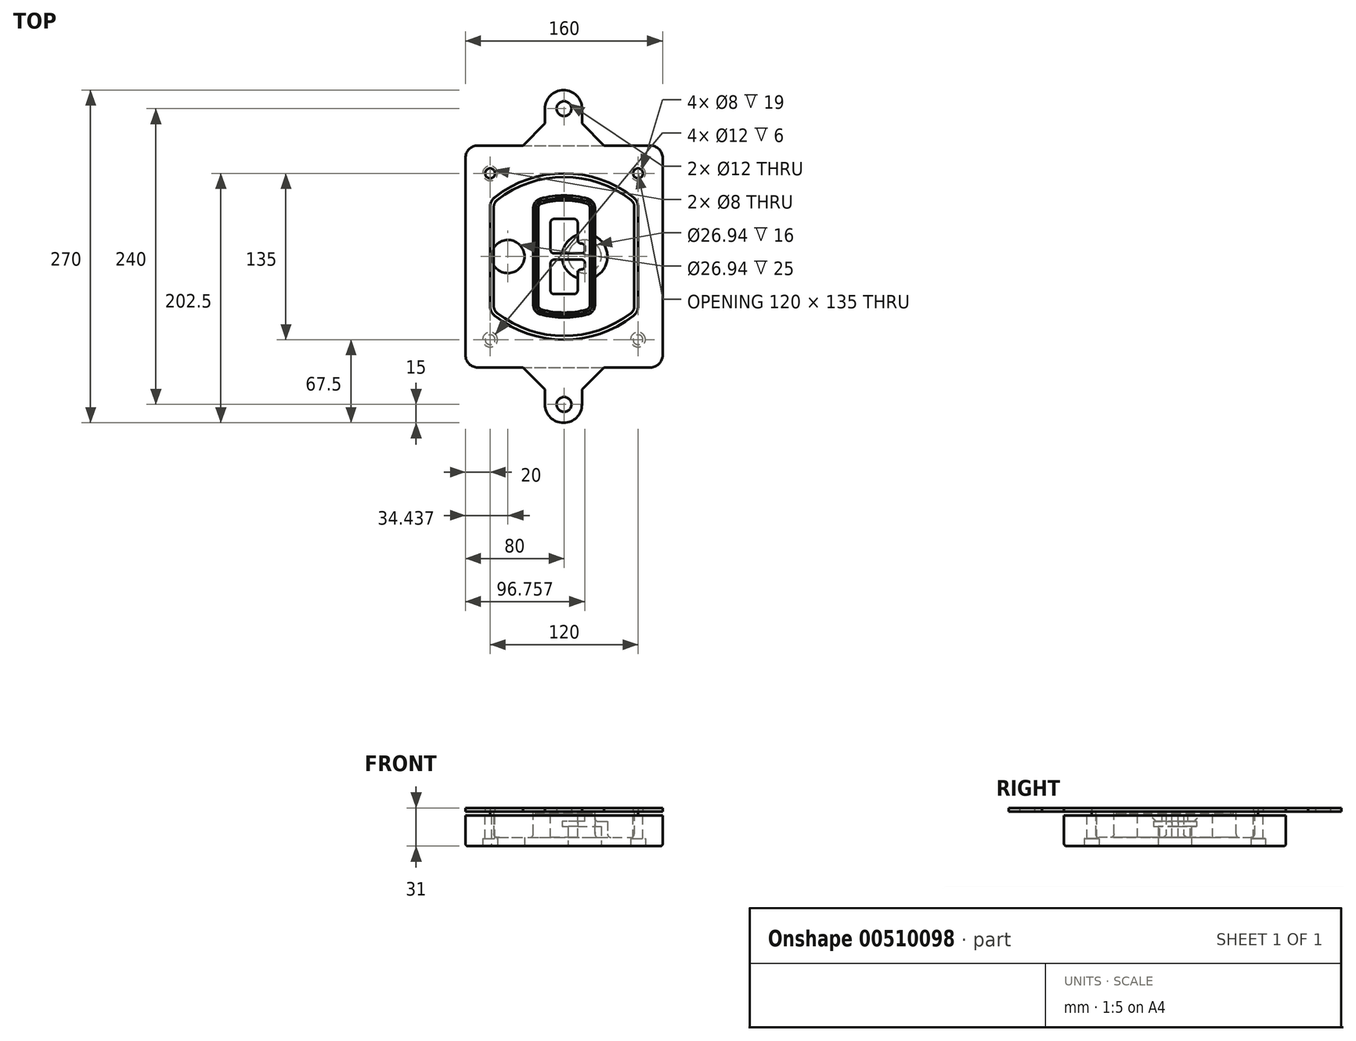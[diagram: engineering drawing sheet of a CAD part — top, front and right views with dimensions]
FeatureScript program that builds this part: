
annotation { "Feature Type Name" : "Feature", "Feature Type Description" : "" }
export const myFeature = defineFeature(function(context is Context, id is Id, definition is map)
    precondition{}
    {
        {
            var Q0;
            Q0=qCreatedBy(makeId("Top.planeOp"),FACE);
            var sketch = newSketch(context, id + "F0", { "sketchPlane" : qUnion([Q0])});
            skPoint(sketch, "E0.rect.middle", {"position": v(0, 0) * mm});
            skLineSegment(sketch, "E1.bottom", {"start": v(-70, -90) * mm, "end": v(70, -90) * mm});
            skLineSegment(sketch, "E1.top", {"start": v(-70, 90) * mm, "end": v(70, 90) * mm});
            skLineSegment(sketch, "E1.left", {"start": v(-80, -80) * mm, "end": v(-80, 80) * mm});
            skLineSegment(sketch, "E1.right", {"start": v(80, -80) * mm, "end": v(80, 80) * mm});
            skLineSegment(sketch, "E2", {"start": v(-80, 90) * mm, "end": v(80, -90) * mm, "construction": true});
            skLineSegment(sketch, "E3", {"start": v(80, 90) * mm, "end": v(-80, -90) * mm, "construction": true});
            skCircle(sketch, "E4", {"center": v(-60, 67.5) * mm, "radius": 4 * mm});
            skCircle(sketch, "E5", {"center": v(60, 67.5) * mm, "radius": 4 * mm});
            skCircle(sketch, "E6", {"center": v(60, -67.5) * mm, "radius": 4 * mm});
            skCircle(sketch, "E7", {"center": v(-60, -67.5) * mm, "radius": 4 * mm});
            skLineSegment(sketch, "E8", {"start": v(-60, 67.5) * mm, "end": v(60, 67.5) * mm, "construction": true});
            skLineSegment(sketch, "E9", {"start": v(60, 67.5) * mm, "end": v(60, -67.5) * mm, "construction": true});
            skLineSegment(sketch, "E10", {"start": v(60, -67.5) * mm, "end": v(-60, -67.5) * mm, "construction": true});
            skLineSegment(sketch, "E11", {"start": v(-60, -67.5) * mm, "end": v(-60, 67.5) * mm, "construction": true});
            skLineSegment(sketch, "E12", {"start": v(-60, 40.3) * mm, "end": v(-60, -40.3) * mm});
            skLineSegment(sketch, "E13", {"start": v(60, 40.3) * mm, "end": v(60, -40.3) * mm});
            skArc(sketch, "E14", {"start": v(56.15, 48.18) * mm, "mid": v(0, 67.5) * mm, "end": v(-56.15, 48.18) * mm});
            skArc(sketch, "E15", {"start": v(-56.15, -48.18) * mm, "mid": v(0, -67.5) * mm, "end": v(56.15, -48.18) * mm});
            skLineSegment(sketch, "E16", {"start": v(-60, 0) * mm, "end": v(60, 0) * mm, "construction": true});
            skPoint(sketch, "E17.visualSharp", {"position": v(-60, -45) * mm});
            skArc(sketch, "E17.filletArc", {"start": v(-60, -40.3) * mm, "mid": v(-58.99, -44.68) * mm, "end": v(-56.15, -48.18) * mm});
            skPoint(sketch, "E18.visualSharp", {"position": v(-60, 45) * mm});
            skArc(sketch, "E18.filletArc", {"start": v(-56.15, 48.18) * mm, "mid": v(-58.99, 44.68) * mm, "end": v(-60, 40.3) * mm});
            skPoint(sketch, "E19.visualSharp", {"position": v(60, 45) * mm});
            skArc(sketch, "E19.filletArc", {"start": v(60, 40.3) * mm, "mid": v(58.99, 44.68) * mm, "end": v(56.15, 48.18) * mm});
            skPoint(sketch, "E20.visualSharp", {"position": v(60, -45) * mm});
            skArc(sketch, "E20.filletArc", {"start": v(56.15, -48.18) * mm, "mid": v(58.99, -44.68) * mm, "end": v(60, -40.3) * mm});
            skPoint(sketch, "E21.visualSharp", {"position": v(-80, 90) * mm});
            skArc(sketch, "E21.filletArc", {"start": v(-70, 90) * mm, "mid": v(-77.07, 87.07) * mm, "end": v(-80, 80) * mm});
            skPoint(sketch, "E22.visualSharp", {"position": v(80, 90) * mm});
            skArc(sketch, "E22.filletArc", {"start": v(80, 80) * mm, "mid": v(77.07, 87.07) * mm, "end": v(70, 90) * mm});
            skPoint(sketch, "E23.visualSharp", {"position": v(80, -90) * mm});
            skArc(sketch, "E23.filletArc", {"start": v(70, -90) * mm, "mid": v(77.07, -87.07) * mm, "end": v(80, -80) * mm});
            skPoint(sketch, "E24.visualSharp", {"position": v(-80, -90) * mm});
            skArc(sketch, "E24.filletArc", {"start": v(-80, -80) * mm, "mid": v(-77.07, -87.07) * mm, "end": v(-70, -90) * mm});
            skArc(sketch, "E25.0", {"start": v(57, 40.3) * mm, "mid": v(56.3, 43.36) * mm, "end": v(54.3, 45.81) * mm});
            skLineSegment(sketch, "E25.1", {"start": v(57, 40.3) * mm, "end": v(57, -40.3) * mm});
            skArc(sketch, "E25.2", {"start": v(54.3, -45.81) * mm, "mid": v(56.3, -43.36) * mm, "end": v(57, -40.3) * mm});
            skArc(sketch, "E25.3", {"start": v(-54.3, -45.81) * mm, "mid": v(0, -64.5) * mm, "end": v(54.3, -45.81) * mm});
            skArc(sketch, "E25.4", {"start": v(-57, -40.3) * mm, "mid": v(-56.3, -43.36) * mm, "end": v(-54.3, -45.81) * mm});
            skArc(sketch, "E25.5", {"start": v(54.3, 45.81) * mm, "mid": v(0, 64.5) * mm, "end": v(-54.3, 45.81) * mm});
            skLineSegment(sketch, "E25.6", {"start": v(-57, 40.3) * mm, "end": v(-57, -40.3) * mm});
            skArc(sketch, "E25.7", {"start": v(-54.3, 45.81) * mm, "mid": v(-56.3, 43.36) * mm, "end": v(-57, 40.3) * mm});
            skArc(sketch, "E26.0", {"start": v(-58.62, 51.33) * mm, "mid": v(-62.58, 46.43) * mm, "end": v(-64, 40.3) * mm});
            skArc(sketch, "E26.1", {"start": v(58.62, 51.33) * mm, "mid": v(0, 71.5) * mm, "end": v(-58.62, 51.33) * mm});
            skArc(sketch, "E26.2", {"start": v(64, 40.3) * mm, "mid": v(62.58, 46.43) * mm, "end": v(58.62, 51.33) * mm});
            skLineSegment(sketch, "E26.3", {"start": v(64, 40.3) * mm, "end": v(64, -40.3) * mm});
            skArc(sketch, "E26.4", {"start": v(58.62, -51.33) * mm, "mid": v(62.58, -46.43) * mm, "end": v(64, -40.3) * mm});
            skLineSegment(sketch, "E26.5", {"start": v(-64, 40.3) * mm, "end": v(-64, -40.3) * mm});
            skArc(sketch, "E26.6", {"start": v(-58.62, -51.33) * mm, "mid": v(0, -71.5) * mm, "end": v(58.62, -51.33) * mm});
            skArc(sketch, "E26.7", {"start": v(-64, -40.3) * mm, "mid": v(-62.58, -46.43) * mm, "end": v(-58.62, -51.33) * mm});
            skSolve(sketch);
        }
        {
            var Q0;
            Q0=makeQuery(id+"F0.imprint","IMPRINT",FACE,{"disambiguationData":[TD([[makeQuery(id+"F0.imprint","IMPRINT",EDGE,{"derivedFrom":sQuery(id+"F0.wireOp",EDGE,"E1.bottom")}),1.0]])]});
            var Q1;
            Q1=makeQuery(id+"F0.imprint","IMPRINT",FACE,{"disambiguationData":[TD([[makeQuery(id+"F0.imprint","IMPRINT",EDGE,{"derivedFrom":sQuery(id+"F0.wireOp",EDGE,"E12")}),1.0]])]});
            var Q2;
            Q2=makeQuery(id+"F0.imprint","IMPRINT",FACE,{"disambiguationData":[TD([[makeQuery(id+"F0.imprint","IMPRINT",EDGE,{"derivedFrom":sQuery(id+"F0.wireOp",EDGE,"E25.0")}),1.0]])]});
            var Q3;
            Q3=makeQuery(id+"F0.imprint","IMPRINT",FACE,{"disambiguationData":[TD([[makeQuery(id+"F0.imprint","IMPRINT",EDGE,{"derivedFrom":sQuery(id+"F0.wireOp",EDGE,"E12")}),-1.0]])]});
            extrude(context, id + "F1", {"entities" : qUnion([Q0, Q1, Q2, Q3]), "oppositeDirection" : true, "depth" : 25 * mm});
        }
        {
            var Q0;
            Q0=makeQuery(id+"F0.imprint","IMPRINT",FACE,{"disambiguationData":[TD([[makeQuery(id+"F0.imprint","IMPRINT",EDGE,{"derivedFrom":sQuery(id+"F0.wireOp",EDGE,"E12")}),1.0]])]});
            extrude(context, id + "F2", {"entities" : qUnion([Q0]), "operationType" : NewBodyOperationType.ADD, "depth" : 3 * mm});
        }
        {
            var Q0;
            Q0=makeQuery(id+"F0.imprint","IMPRINT",FACE,{"disambiguationData":[TD([[makeQuery(id+"F0.imprint","IMPRINT",EDGE,{"derivedFrom":sQuery(id+"F0.wireOp",EDGE,"E25.0")}),1.0]])]});
            extrude(context, id + "F3", {"entities" : qUnion([Q0]), "operationType" : NewBodyOperationType.REMOVE, "oppositeDirection" : true, "depth" : 18 * mm});
        }
        {
            var Q0;
            Q0=makeQuery(id+"F2.opExtrude","CAP_FACE",FACE,{"disambiguationData":[OSD([sQuery(id+"F0.wireOp",EDGE,"E12"),sQuery(id+"F0.wireOp",EDGE,"E13"),sQuery(id+"F0.wireOp",EDGE,"E14"),sQuery(id+"F0.wireOp",EDGE,"E15"),sQuery(id+"F0.wireOp",EDGE,"E17.filletArc"),sQuery(id+"F0.wireOp",EDGE,"E18.filletArc"),sQuery(id+"F0.wireOp",EDGE,"E19.filletArc"),sQuery(id+"F0.wireOp",EDGE,"E20.filletArc"),sQuery(id+"F0.wireOp",EDGE,"E25.0"),sQuery(id+"F0.wireOp",EDGE,"E25.1"),sQuery(id+"F0.wireOp",EDGE,"E25.2"),sQuery(id+"F0.wireOp",EDGE,"E25.3"),sQuery(id+"F0.wireOp",EDGE,"E25.4"),sQuery(id+"F0.wireOp",EDGE,"E25.5"),sQuery(id+"F0.wireOp",EDGE,"E25.6"),sQuery(id+"F0.wireOp",EDGE,"E25.7")])],"isStart":false});
            var sketch = newSketch(context, id + "F4", { "sketchPlane" : qUnion([Q0])});
            skArc(sketch, "E27.0", {"start": v(-19.08, -46.97) * mm, "mid": v(0, -49.5) * mm, "end": v(19.08, -46.97) * mm});
            skArc(sketch, "E28.0", {"start": v(19.08, 46.97) * mm, "mid": v(0, 49.5) * mm, "end": v(-19.08, 46.97) * mm});
            skLineSegment(sketch, "E29", {"start": v(-25, 39.25) * mm, "end": v(-25, -39.25) * mm});
            skLineSegment(sketch, "E30", {"start": v(25, 39.25) * mm, "end": v(25, -39.25) * mm});
            skLineSegment(sketch, "E31", {"start": v(-25, 45.1) * mm, "end": v(25, 45.1) * mm, "construction": true});
            skLineSegment(sketch, "E32", {"start": v(-25, -45.1) * mm, "end": v(25, -45.1) * mm, "construction": true});
            skPoint(sketch, "E33.visualSharp", {"position": v(-25, 45.1) * mm});
            skArc(sketch, "E33.filletArc", {"start": v(-19.08, 46.97) * mm, "mid": v(-23.35, 44.11) * mm, "end": v(-25, 39.25) * mm});
            skPoint(sketch, "E34.visualSharp", {"position": v(25, 45.1) * mm});
            skArc(sketch, "E34.filletArc", {"start": v(25, 39.25) * mm, "mid": v(23.35, 44.11) * mm, "end": v(19.08, 46.97) * mm});
            skPoint(sketch, "E35.visualSharp", {"position": v(25, -45.1) * mm});
            skArc(sketch, "E35.filletArc", {"start": v(19.08, -46.97) * mm, "mid": v(23.35, -44.11) * mm, "end": v(25, -39.25) * mm});
            skPoint(sketch, "E36.visualSharp", {"position": v(-25, -45.1) * mm});
            skArc(sketch, "E36.filletArc", {"start": v(-25, -39.25) * mm, "mid": v(-23.35, -44.11) * mm, "end": v(-19.08, -46.97) * mm});
            skArc(sketch, "E37.0", {"start": v(54.3, 45.81) * mm, "mid": v(0, 64.5) * mm, "end": v(-54.3, 45.81) * mm});
            skArc(sketch, "E37.1", {"start": v(-54.3, 45.81) * mm, "mid": v(-56.3, 43.36) * mm, "end": v(-57, 40.3) * mm});
            skLineSegment(sketch, "E37.2", {"start": v(-57, 40.3) * mm, "end": v(-57, -40.3) * mm});
            skArc(sketch, "E37.3", {"start": v(-57, -40.3) * mm, "mid": v(-56.3, -43.36) * mm, "end": v(-54.3, -45.81) * mm});
            skArc(sketch, "E37.4", {"start": v(-54.3, -45.81) * mm, "mid": v(0, -64.5) * mm, "end": v(54.3, -45.81) * mm});
            skArc(sketch, "E37.5", {"start": v(54.3, -45.81) * mm, "mid": v(56.3, -43.36) * mm, "end": v(57, -40.3) * mm});
            skLineSegment(sketch, "E37.6", {"start": v(57, 40.3) * mm, "end": v(57, -40.3) * mm});
            skArc(sketch, "E37.7", {"start": v(57, 40.3) * mm, "mid": v(56.3, 43.36) * mm, "end": v(54.3, 45.81) * mm});
            skLineSegment(sketch, "E38.0", {"start": v(23, 39.25) * mm, "end": v(23, -39.25) * mm});
            skArc(sketch, "E38.1", {"start": v(18.56, -45.04) * mm, "mid": v(21.76, -42.9) * mm, "end": v(23, -39.25) * mm});
            skArc(sketch, "E38.2", {"start": v(-18.56, -45.04) * mm, "mid": v(0, -47.5) * mm, "end": v(18.56, -45.04) * mm});
            skArc(sketch, "E38.3", {"start": v(-23, -39.25) * mm, "mid": v(-21.76, -42.9) * mm, "end": v(-18.56, -45.04) * mm});
            skLineSegment(sketch, "E38.4", {"start": v(-23, 39.25) * mm, "end": v(-23, -39.25) * mm});
            skArc(sketch, "E38.5", {"start": v(23, 39.25) * mm, "mid": v(21.76, 42.9) * mm, "end": v(18.56, 45.04) * mm});
            skArc(sketch, "E38.6", {"start": v(-18.56, 45.04) * mm, "mid": v(-21.76, 42.9) * mm, "end": v(-23, 39.25) * mm});
            skArc(sketch, "E38.7", {"start": v(18.56, 45.04) * mm, "mid": v(0, 47.5) * mm, "end": v(-18.56, 45.04) * mm});
            skArc(sketch, "E39.0", {"start": v(21, 39.25) * mm, "mid": v(20.18, 41.68) * mm, "end": v(18.04, 43.1) * mm});
            skLineSegment(sketch, "E39.1", {"start": v(21, 39.25) * mm, "end": v(21, -39.25) * mm});
            skArc(sketch, "E39.2", {"start": v(18.04, -43.1) * mm, "mid": v(20.18, -41.68) * mm, "end": v(21, -39.25) * mm});
            skArc(sketch, "E39.3", {"start": v(-18.04, -43.1) * mm, "mid": v(0, -45.5) * mm, "end": v(18.04, -43.1) * mm});
            skArc(sketch, "E39.4", {"start": v(-21, -39.25) * mm, "mid": v(-20.18, -41.68) * mm, "end": v(-18.04, -43.1) * mm});
            skArc(sketch, "E39.5", {"start": v(18.04, 43.1) * mm, "mid": v(0, 45.5) * mm, "end": v(-18.04, 43.1) * mm});
            skLineSegment(sketch, "E39.6", {"start": v(-21, 39.25) * mm, "end": v(-21, -39.25) * mm});
            skArc(sketch, "E39.7", {"start": v(-18.04, 43.1) * mm, "mid": v(-20.18, 41.68) * mm, "end": v(-21, 39.25) * mm});
            skLineSegment(sketch, "E40", {"start": v(-25, 0) * mm, "end": v(25, 0) * mm, "construction": true});
            skLineSegment(sketch, "E41", {"start": v(-11, 5.5) * mm, "end": v(-11, 27.5) * mm});
            skLineSegment(sketch, "E42", {"start": v(-8, 30.5) * mm, "end": v(8, 30.5) * mm});
            skLineSegment(sketch, "E43", {"start": v(11, 27.5) * mm, "end": v(11, 13.5) * mm});
            skLineSegment(sketch, "E44", {"start": v(14, 10.5) * mm, "end": v(14, 10.5) * mm});
            skLineSegment(sketch, "E45", {"start": v(17, 7.5) * mm, "end": v(17, 5.5) * mm});
            skLineSegment(sketch, "E46", {"start": v(14, 2.5) * mm, "end": v(-8, 2.5) * mm});
            skPoint(sketch, "E47.visualSharp", {"position": v(-11, 30.5) * mm});
            skArc(sketch, "E47.filletArc", {"start": v(-8, 30.5) * mm, "mid": v(-10.12, 29.62) * mm, "end": v(-11, 27.5) * mm});
            skPoint(sketch, "E48.visualSharp", {"position": v(11, 30.5) * mm});
            skArc(sketch, "E48.filletArc", {"start": v(11, 27.5) * mm, "mid": v(10.12, 29.62) * mm, "end": v(8, 30.5) * mm});
            skPoint(sketch, "E49.visualSharp", {"position": v(11, 10.5) * mm});
            skArc(sketch, "E49.filletArc", {"start": v(11, 13.5) * mm, "mid": v(11.88, 11.38) * mm, "end": v(14, 10.5) * mm});
            skPoint(sketch, "E50.visualSharp", {"position": v(17, 10.5) * mm});
            skArc(sketch, "E50.filletArc", {"start": v(17, 7.5) * mm, "mid": v(16.12, 9.62) * mm, "end": v(14, 10.5) * mm});
            skPoint(sketch, "E51.visualSharp", {"position": v(17, 2.5) * mm});
            skArc(sketch, "E51.filletArc", {"start": v(14, 2.5) * mm, "mid": v(16.12, 3.38) * mm, "end": v(17, 5.5) * mm});
            skPoint(sketch, "E52.visualSharp", {"position": v(-11, 2.5) * mm});
            skArc(sketch, "E52.filletArc", {"start": v(-11, 5.5) * mm, "mid": v(-10.12, 3.38) * mm, "end": v(-8, 2.5) * mm});
            skLineSegment(sketch, "E53.0.MirrorCS", {"start": v(14, -2.5) * mm, "end": v(-8, -2.5) * mm});
            skArc(sketch, "E54.0.MirrorCS", {"start": v(-11, -5.5) * mm, "mid": v(-10.12, -3.38) * mm, "end": v(-8, -2.5) * mm});
            skLineSegment(sketch, "E55.0.MirrorCS", {"start": v(-11, -5.5) * mm, "end": v(-11, -27.5) * mm});
            skArc(sketch, "E56.0.MirrorCS", {"start": v(-8, -30.5) * mm, "mid": v(-10.12, -29.62) * mm, "end": v(-11, -27.5) * mm});
            skLineSegment(sketch, "E57.0.MirrorCS", {"start": v(-8, -30.5) * mm, "end": v(8, -30.5) * mm});
            skArc(sketch, "E58.0.MirrorCS", {"start": v(11, -27.5) * mm, "mid": v(10.12, -29.62) * mm, "end": v(8, -30.5) * mm});
            skLineSegment(sketch, "E59.0.MirrorCS", {"start": v(11, -27.5) * mm, "end": v(11, -13.5) * mm});
            skArc(sketch, "E60.0.MirrorCS", {"start": v(11, -13.5) * mm, "mid": v(11.88, -11.38) * mm, "end": v(14, -10.5) * mm});
            skArc(sketch, "E61.0.MirrorCS", {"start": v(17, -7.5) * mm, "mid": v(16.12, -9.62) * mm, "end": v(14, -10.5) * mm});
            skLineSegment(sketch, "E62.0.MirrorCS", {"start": v(17, -7.5) * mm, "end": v(17, -5.5) * mm});
            skArc(sketch, "E63.0.MirrorCS", {"start": v(14, -2.5) * mm, "mid": v(16.12, -3.38) * mm, "end": v(17, -5.5) * mm});
            skSolve(sketch);
        }
        {
            var Q0;
            Q0=makeQuery(id+"F4.imprint","IMPRINT",FACE,{"disambiguationData":[TD([[makeQuery(id+"F4.imprint","IMPRINT",EDGE,{"derivedFrom":sQuery(id+"F4.wireOp",EDGE,"E27.0")}),1.0]])]});
            var Q1;
            Q1=makeQuery(id+"F4.imprint","IMPRINT",FACE,{"disambiguationData":[TD([[makeQuery(id+"F4.imprint","IMPRINT",EDGE,{"derivedFrom":sQuery(id+"F4.wireOp",EDGE,"E38.0")}),-1.0]])]});
            var Q2;
            Q2=makeQuery(id+"F4.imprint","IMPRINT",FACE,{"disambiguationData":[TD([[makeQuery(id+"F4.imprint","IMPRINT",EDGE,{"derivedFrom":sQuery(id+"F4.wireOp",EDGE,"E39.0")}),1.0]])]});
            extrude(context, id + "F5", {"entities" : qUnion([Q0, Q1, Q2]), "operationType" : NewBodyOperationType.ADD, "endBound" : BoundingType.UP_TO_NEXT, "oppositeDirection" : true, "depth" : 25 * mm});
        }
        {
            var Q0;
            Q0=makeQuery(id+"F4.imprint","IMPRINT",FACE,{"disambiguationData":[TD([[makeQuery(id+"F4.imprint","IMPRINT",EDGE,{"derivedFrom":sQuery(id+"F4.wireOp",EDGE,"E38.0")}),-1.0]])]});
            extrude(context, id + "F6", {"entities" : qUnion([Q0]), "operationType" : NewBodyOperationType.REMOVE, "oppositeDirection" : true, "depth" : 2 * mm});
        }
        {
            var Q0;
            Q0=makeQuery(id+"F1.opExtrude","CAP_FACE",FACE,{"disambiguationData":[OSD([sQuery(id+"F0.wireOp",EDGE,"E1.bottom"),sQuery(id+"F0.wireOp",EDGE,"E1.top"),sQuery(id+"F0.wireOp",EDGE,"E1.left"),sQuery(id+"F0.wireOp",EDGE,"E1.right"),sQuery(id+"F0.wireOp",EDGE,"E4"),sQuery(id+"F0.wireOp",EDGE,"E5"),sQuery(id+"F0.wireOp",EDGE,"E6"),sQuery(id+"F0.wireOp",EDGE,"E7"),sQuery(id+"F0.wireOp",EDGE,"E21.filletArc"),sQuery(id+"F0.wireOp",EDGE,"E22.filletArc"),sQuery(id+"F0.wireOp",EDGE,"E23.filletArc"),sQuery(id+"F0.wireOp",EDGE,"E24.filletArc")])],"isStart":false});
            var sketch = newSketch(context, id + "F7", { "sketchPlane" : qUnion([Q0])});
            skCircle(sketch, "E64", {"center": v(16.76, 0) * mm, "radius": 13.47 * mm});
            skCircle(sketch, "E65", {"center": v(-45.56, 0) * mm, "radius": 13.47 * mm});
            skLineSegment(sketch, "E66", {"start": v(80, 0) * mm, "end": v(-80, 0) * mm});
            skCircle(sketch, "E67", {"center": v(16.76, 0) * mm, "radius": 18.47 * mm});
            skCircle(sketch, "E68", {"center": v(60, -67.5) * mm, "radius": 6 * mm});
            skCircle(sketch, "E69", {"center": v(-60, -67.5) * mm, "radius": 6 * mm});
            skCircle(sketch, "E70", {"center": v(-60, 67.5) * mm, "radius": 6 * mm});
            skCircle(sketch, "E71", {"center": v(60, 67.5) * mm, "radius": 6 * mm});
            skSolve(sketch);
        }
        {
            var Q0;
            {var subQ1=sQuery(id+"F7.wireOp",EDGE,"E66");var subQ4=sQuery(id+"F7.wireOp",EDGE,"E64");var subQ6=makeQuery(id+"F7.imprint","INTERSECT",VERTEX,{"disambiguationData":[OD(0.0)],"derivedFrom":[subQ4,subQ1]});Q0=makeQuery(id+"F7.imprint","IMPRINT",FACE,{"disambiguationData":[TD([[makeQuery(id+"F7.imprint","IMPRINT",EDGE,{"disambiguationData":[TD([[subQ6,-1.0]])],"derivedFrom":subQ4}),-1.0]])]});}
            var Q1;
            {var subQ0=sQuery(id+"F7.wireOp",EDGE,"E66");var subQ1=sQuery(id+"F7.wireOp",EDGE,"E64");var subQ3=makeQuery(id+"F7.imprint","INTERSECT",VERTEX,{"disambiguationData":[OD(0.0)],"derivedFrom":[subQ1,subQ0]});Q1=makeQuery(id+"F7.imprint","IMPRINT",FACE,{"disambiguationData":[TD([[makeQuery(id+"F7.imprint","IMPRINT",EDGE,{"disambiguationData":[TD([[subQ3,-1.0]])],"derivedFrom":subQ1}),1.0]])]});}
            var Q2;
            {var subQ0=sQuery(id+"F7.wireOp",EDGE,"E66");var subQ1=sQuery(id+"F7.wireOp",EDGE,"E64");var subQ3=makeQuery(id+"F7.imprint","INTERSECT",VERTEX,{"disambiguationData":[OD(0.0)],"derivedFrom":[subQ1,subQ0]});Q2=makeQuery(id+"F7.imprint","IMPRINT",FACE,{"disambiguationData":[TD([[makeQuery(id+"F7.imprint","IMPRINT",EDGE,{"disambiguationData":[TD([[subQ3,1.0]])],"derivedFrom":subQ1}),1.0]])]});}
            var Q3;
            {var subQ1=sQuery(id+"F7.wireOp",EDGE,"E66");var subQ4=sQuery(id+"F7.wireOp",EDGE,"E64");var subQ6=makeQuery(id+"F7.imprint","INTERSECT",VERTEX,{"disambiguationData":[OD(0.0)],"derivedFrom":[subQ4,subQ1]});Q3=makeQuery(id+"F7.imprint","IMPRINT",FACE,{"disambiguationData":[TD([[makeQuery(id+"F7.imprint","IMPRINT",EDGE,{"disambiguationData":[TD([[subQ6,1.0]])],"derivedFrom":subQ4}),-1.0]])]});}
            extrude(context, id + "F8", {"entities" : qUnion([Q0, Q1, Q2, Q3]), "operationType" : NewBodyOperationType.ADD, "oppositeDirection" : true, "depth" : 20 * mm});
        }
        {
            var Q0;
            {var subQ0=sQuery(id+"F7.wireOp",EDGE,"E66");var subQ1=sQuery(id+"F7.wireOp",EDGE,"E64");var subQ3=makeQuery(id+"F7.imprint","INTERSECT",VERTEX,{"disambiguationData":[OD(0.0)],"derivedFrom":[subQ1,subQ0]});Q0=makeQuery(id+"F7.imprint","IMPRINT",FACE,{"disambiguationData":[TD([[makeQuery(id+"F7.imprint","IMPRINT",EDGE,{"disambiguationData":[TD([[subQ3,-1.0]])],"derivedFrom":subQ1}),1.0]])]});}
            var Q1;
            {var subQ0=sQuery(id+"F7.wireOp",EDGE,"E66");var subQ1=sQuery(id+"F7.wireOp",EDGE,"E64");var subQ3=makeQuery(id+"F7.imprint","INTERSECT",VERTEX,{"disambiguationData":[OD(0.0)],"derivedFrom":[subQ1,subQ0]});Q1=makeQuery(id+"F7.imprint","IMPRINT",FACE,{"disambiguationData":[TD([[makeQuery(id+"F7.imprint","IMPRINT",EDGE,{"disambiguationData":[TD([[subQ3,1.0]])],"derivedFrom":subQ1}),1.0]])]});}
            extrude(context, id + "F9", {"entities" : qUnion([Q0, Q1]), "operationType" : NewBodyOperationType.REMOVE, "oppositeDirection" : true, "depth" : 16 * mm});
        }
        {
            var Q0;
            {var subQ0=sQuery(id+"F7.wireOp",EDGE,"E66");var subQ1=sQuery(id+"F7.wireOp",EDGE,"E65");var subQ3=makeQuery(id+"F7.imprint","INTERSECT",VERTEX,{"disambiguationData":[OD(0.0)],"derivedFrom":[subQ1,subQ0]});Q0=makeQuery(id+"F7.imprint","IMPRINT",FACE,{"disambiguationData":[TD([[makeQuery(id+"F7.imprint","IMPRINT",EDGE,{"disambiguationData":[TD([[subQ3,-1.0]])],"derivedFrom":subQ1}),1.0]])]});}
            var Q1;
            {var subQ0=sQuery(id+"F7.wireOp",EDGE,"E66");var subQ1=sQuery(id+"F7.wireOp",EDGE,"E65");var subQ3=makeQuery(id+"F7.imprint","INTERSECT",VERTEX,{"disambiguationData":[OD(0.0)],"derivedFrom":[subQ1,subQ0]});Q1=makeQuery(id+"F7.imprint","IMPRINT",FACE,{"disambiguationData":[TD([[makeQuery(id+"F7.imprint","IMPRINT",EDGE,{"disambiguationData":[TD([[subQ3,1.0]])],"derivedFrom":subQ1}),1.0]])]});}
            extrude(context, id + "F10", {"entities" : qUnion([Q0, Q1]), "operationType" : NewBodyOperationType.REMOVE, "oppositeDirection" : true, "depth" : 25 * mm});
        }
        {
            var Q0;
            Q0=makeQuery(id+"F7.imprint","IMPRINT",FACE,{"disambiguationData":[TD([[makeQuery(id+"F7.imprint","IMPRINT",EDGE,{"derivedFrom":sQuery(id+"F7.wireOp",EDGE,"E68")}),1.0]])]});
            var Q1;
            Q1=makeQuery(id+"F7.imprint","IMPRINT",FACE,{"disambiguationData":[TD([[makeQuery(id+"F7.imprint","IMPRINT",EDGE,{"derivedFrom":makeQuery(id+"F1.opExtrude","CAP_EDGE",EDGE,{"disambiguationData":[OSD([sQuery(id+"F0.wireOp",EDGE,"E5")])],"isStart":false})}),-1.0]])]});
            var Q2;
            Q2=makeQuery(id+"F7.imprint","IMPRINT",FACE,{"disambiguationData":[TD([[makeQuery(id+"F7.imprint","IMPRINT",EDGE,{"derivedFrom":sQuery(id+"F7.wireOp",EDGE,"E69")}),1.0]])]});
            var Q3;
            Q3=makeQuery(id+"F7.imprint","IMPRINT",FACE,{"disambiguationData":[TD([[makeQuery(id+"F7.imprint","IMPRINT",EDGE,{"derivedFrom":makeQuery(id+"F1.opExtrude","CAP_EDGE",EDGE,{"disambiguationData":[OSD([sQuery(id+"F0.wireOp",EDGE,"E4")])],"isStart":false})}),-1.0]])]});
            var Q4;
            Q4=makeQuery(id+"F7.imprint","IMPRINT",FACE,{"disambiguationData":[TD([[makeQuery(id+"F7.imprint","IMPRINT",EDGE,{"derivedFrom":sQuery(id+"F7.wireOp",EDGE,"E70")}),1.0]])]});
            var Q5;
            Q5=makeQuery(id+"F7.imprint","IMPRINT",FACE,{"disambiguationData":[TD([[makeQuery(id+"F7.imprint","IMPRINT",EDGE,{"derivedFrom":makeQuery(id+"F1.opExtrude","CAP_EDGE",EDGE,{"disambiguationData":[OSD([sQuery(id+"F0.wireOp",EDGE,"E7")])],"isStart":false})}),-1.0]])]});
            var Q6;
            Q6=makeQuery(id+"F7.imprint","IMPRINT",FACE,{"disambiguationData":[TD([[makeQuery(id+"F7.imprint","IMPRINT",EDGE,{"derivedFrom":sQuery(id+"F7.wireOp",EDGE,"E71")}),1.0]])]});
            var Q7;
            Q7=makeQuery(id+"F7.imprint","IMPRINT",FACE,{"disambiguationData":[TD([[makeQuery(id+"F7.imprint","IMPRINT",EDGE,{"derivedFrom":makeQuery(id+"F1.opExtrude","CAP_EDGE",EDGE,{"disambiguationData":[OSD([sQuery(id+"F0.wireOp",EDGE,"E6")])],"isStart":false})}),-1.0]])]});
            extrude(context, id + "F11", {"entities" : qUnion([Q0, Q1, Q2, Q3, Q4, Q5, Q6, Q7]), "operationType" : NewBodyOperationType.REMOVE, "oppositeDirection" : true, "depth" : 6 * mm});
        }
        {
            var Q0;
            Q0=makeQuery(id+"F9.boolean.opBoolean","COPY",FACE,{"derivedFrom":makeQuery(id+"F9.opExtrude","CAP_FACE",FACE,{"disambiguationData":[OSD([sQuery(id+"F7.wireOp",EDGE,"E64")])],"isStart":false})});
            var sketch = newSketch(context, id + "F12", { "sketchPlane" : qUnion([Q0])});
            skArc(sketch, "E72.0", {"start": v(11, 17.55) * mm, "mid": v(2.57, 11.82) * mm, "end": v(-1.54, 2.5) * mm});
            skArc(sketch, "E72.1", {"start": v(-1.54, -2.5) * mm, "mid": v(2.57, -11.82) * mm, "end": v(11, -17.55) * mm});
            skLineSegment(sketch, "E73", {"start": v(-1.54, -2.5) * mm, "end": v(14, -2.5) * mm});
            skLineSegment(sketch, "E74.0", {"start": v(14, 2.5) * mm, "end": v(-1.54, 2.5) * mm});
            skArc(sketch, "E74.1", {"start": v(14, 2.5) * mm, "mid": v(16.12, 3.38) * mm, "end": v(17, 5.5) * mm});
            skLineSegment(sketch, "E74.2", {"start": v(17, 7.5) * mm, "end": v(17, 5.5) * mm});
            skArc(sketch, "E74.3", {"start": v(17, 7.5) * mm, "mid": v(16.12, 9.62) * mm, "end": v(14, 10.5) * mm});
            skArc(sketch, "E74.4", {"start": v(11, 13.5) * mm, "mid": v(11.88, 11.38) * mm, "end": v(14, 10.5) * mm});
            skLineSegment(sketch, "E74.5", {"start": v(11, 17.55) * mm, "end": v(11, 13.5) * mm});
            skLineSegment(sketch, "E74.7", {"start": v(14, -2.5) * mm, "end": v(-1.54, -2.5) * mm});
            skArc(sketch, "E74.8", {"start": v(14, -2.5) * mm, "mid": v(16.12, -3.38) * mm, "end": v(17, -5.5) * mm});
            skLineSegment(sketch, "E74.9", {"start": v(17, -7.5) * mm, "end": v(17, -5.5) * mm});
            skArc(sketch, "E74.10", {"start": v(17, -7.5) * mm, "mid": v(16.12, -9.62) * mm, "end": v(14, -10.5) * mm});
            skArc(sketch, "E74.11", {"start": v(11, -13.5) * mm, "mid": v(11.88, -11.38) * mm, "end": v(14, -10.5) * mm});
            skLineSegment(sketch, "E74.12", {"start": v(11, -17.55) * mm, "end": v(11, -13.5) * mm});
            skPoint(sketch, "E75.orphan", {"position": v(11, -27.5) * mm});
            skPoint(sketch, "E76.orphan", {"position": v(-8, -2.5) * mm});
            skPoint(sketch, "E77.orphan", {"position": v(-8, 2.5) * mm});
            skPoint(sketch, "E78.orphan", {"position": v(11, 27.5) * mm});
            skSolve(sketch);
        }
        {
            var Q0;
            {var subQ7=sQuery(id+"F12.wireOp",EDGE,"E72.0");var subQ14=sQuery(id+"F12.wireOp",EDGE,"E72.1");var subQ16=sQuery(id+"F12.wireOp",EDGE,"E74.1");var subQ18=sQuery(id+"F12.wireOp",EDGE,"E74.8");Q0=qUnion([makeQuery(id+"F12.imprint","IMPRINT",FACE,{"disambiguationData":[TD([[makeQuery(id+"F12.imprint","IMPRINT",EDGE,{"derivedFrom":subQ7}),1.0]])]}),makeQuery(id+"F12.imprint","IMPRINT",FACE,{"disambiguationData":[TD([[makeQuery(id+"F12.imprint","IMPRINT",EDGE,{"derivedFrom":subQ14}),1.0]])]}),makeQuery(id+"F12.imprint","IMPRINT",FACE,{"disambiguationData":[TD([[makeQuery(id+"F12.imprint","IMPRINT",EDGE,{"derivedFrom":subQ16}),1.0]])]}),makeQuery(id+"F12.imprint","IMPRINT",FACE,{"disambiguationData":[TD([[makeQuery(id+"F12.imprint","IMPRINT",EDGE,{"derivedFrom":subQ18}),-1.0]])]})]);}
            var Q1;
            Q1=makeQuery(id+"F5.boolean.opBoolean","SPLIT",FACE,{"disambiguationData":[TD([makeQuery(id+"F5.opExtrude","SWEPT_FACE",FACE,{"disambiguationData":[OSD([sQuery(id+"F4.wireOp",EDGE,"E41")])]})])],"derivedFrom":makeQuery(id+"F3.boolean.opBoolean","COPY",FACE,{"derivedFrom":makeQuery(id+"F3.opExtrude","CAP_FACE",FACE,{"disambiguationData":[OSD([sQuery(id+"F0.wireOp",EDGE,"E25.0"),sQuery(id+"F0.wireOp",EDGE,"E25.1"),sQuery(id+"F0.wireOp",EDGE,"E25.2"),sQuery(id+"F0.wireOp",EDGE,"E25.3"),sQuery(id+"F0.wireOp",EDGE,"E25.4"),sQuery(id+"F0.wireOp",EDGE,"E25.5"),sQuery(id+"F0.wireOp",EDGE,"E25.6"),sQuery(id+"F0.wireOp",EDGE,"E25.7")])],"isStart":false})})});
            extrude(context, id + "F13", {"entities" : qUnion([Q0]), "operationType" : NewBodyOperationType.REMOVE, "endBound" : BoundingType.UP_TO_SURFACE, "endBoundEntityFace" : qUnion([Q1]), "depth" : 25 * mm});
        }
        {
            var Q0;
            Q0=makeQuery(id+"F3.boolean.opBoolean","COPY",EDGE,{"derivedFrom":makeQuery(id+"F3.opExtrude","CAP_EDGE",EDGE,{"disambiguationData":[OSD([sQuery(id+"F0.wireOp",EDGE,"E25.6")])],"isStart":false})});
            var Q1;
            Q1=makeQuery(id+"F8.boolean.opBoolean","INTERSECT",EDGE,{"derivedFrom":[makeQuery(id+"F5.opExtrude","SWEPT_FACE",FACE,{"disambiguationData":[OSD([sQuery(id+"F4.wireOp",EDGE,"E30")])]}),makeQuery(id+"F8.opExtrude","CAP_FACE",FACE,{"disambiguationData":[OSD([sQuery(id+"F7.wireOp",EDGE,"E67")])],"isStart":false})]});
            var Q2;
            Q2=makeQuery(id+"F8.boolean.opBoolean","INTERSECT",EDGE,{"disambiguationData":[OD(1.0)],"derivedFrom":[makeQuery(id+"F5.opExtrude","SWEPT_FACE",FACE,{"disambiguationData":[OSD([sQuery(id+"F4.wireOp",EDGE,"E30")])]}),makeQuery(id+"F8.opExtrude","SWEPT_FACE",FACE,{"disambiguationData":[OSD([sQuery(id+"F7.wireOp",EDGE,"E67")])]})]});
            var Q3;
            {var subQ0=sQuery(id+"F4.wireOp",EDGE,"E30");Q3=makeQuery(id+"F8.boolean.opBoolean","SPLIT",EDGE,{"disambiguationData":[TD([makeQuery(id+"F5.opExtrude","SWEPT_FACE",FACE,{"disambiguationData":[OSD([sQuery(id+"F4.wireOp",EDGE,"E35.filletArc")])]})])],"derivedFrom":makeQuery(id+"F5.opExtrude","CAP_EDGE",EDGE,{"disambiguationData":[OSD([subQ0])],"isStart":false})});}
            var Q4;
            {var subQ0=sQuery(id+"F0.wireOp",EDGE,"E25.7");var subQ1=sQuery(id+"F0.wireOp",EDGE,"E25.1");var subQ2=sQuery(id+"F0.wireOp",EDGE,"E25.6");var subQ3=sQuery(id+"F0.wireOp",EDGE,"E25.5");var subQ4=sQuery(id+"F0.wireOp",EDGE,"E25.4");var subQ5=sQuery(id+"F0.wireOp",EDGE,"E25.0");var subQ6=sQuery(id+"F0.wireOp",EDGE,"E25.2");var subQ7=sQuery(id+"F0.wireOp",EDGE,"E25.3");Q4=makeQuery(id+"F8.boolean.opBoolean","INTERSECT",EDGE,{"derivedFrom":[makeQuery(id+"F5.boolean.opBoolean","SPLIT",FACE,{"disambiguationData":[TD([makeQuery(id+"F2.opExtrude","SWEPT_FACE",FACE,{"disambiguationData":[OSD([subQ5])]})])],"derivedFrom":makeQuery(id+"F3.boolean.opBoolean","COPY",FACE,{"derivedFrom":makeQuery(id+"F3.opExtrude","CAP_FACE",FACE,{"disambiguationData":[OSD([subQ5,subQ1,subQ6,subQ7,subQ4,subQ3,subQ2,subQ0])],"isStart":false})})}),makeQuery(id+"F8.opExtrude","SWEPT_FACE",FACE,{"disambiguationData":[OSD([sQuery(id+"F7.wireOp",EDGE,"E67")])]})]});}
            var Q5;
            Q5=makeQuery(id+"F8.boolean.opBoolean","INTERSECT",EDGE,{"disambiguationData":[OD(0.0)],"derivedFrom":[makeQuery(id+"F5.opExtrude","SWEPT_FACE",FACE,{"disambiguationData":[OSD([sQuery(id+"F4.wireOp",EDGE,"E30")])]}),makeQuery(id+"F8.opExtrude","SWEPT_FACE",FACE,{"disambiguationData":[OSD([sQuery(id+"F7.wireOp",EDGE,"E67")])]})]});
            fillet(context, id + "F14", {"entities" : qUnion([Q0, Q1, Q2, Q3, Q4, Q5]), "radius" : 3 * mm, "tangentPropagation" : true, "allowEdgeOverflow" : false});
        }
        {
            var Q0;
            Q0=makeQuery(id+"F1.opExtrude","CAP_EDGE",EDGE,{"disambiguationData":[OSD([sQuery(id+"F0.wireOp",EDGE,"E1.bottom")])],"isStart":false});
            fillet(context, id + "F15", {"entities" : qUnion([Q0]), "radius" : 2 * mm, "tangentPropagation" : true, "allowEdgeOverflow" : false});
        }
        {
            var Q0;
            Q0=makeQuery(id+"F2.opExtrude","CAP_FACE",FACE,{"disambiguationData":[OSD([sQuery(id+"F0.wireOp",EDGE,"E12"),sQuery(id+"F0.wireOp",EDGE,"E13"),sQuery(id+"F0.wireOp",EDGE,"E14"),sQuery(id+"F0.wireOp",EDGE,"E15"),sQuery(id+"F0.wireOp",EDGE,"E17.filletArc"),sQuery(id+"F0.wireOp",EDGE,"E18.filletArc"),sQuery(id+"F0.wireOp",EDGE,"E19.filletArc"),sQuery(id+"F0.wireOp",EDGE,"E20.filletArc"),sQuery(id+"F0.wireOp",EDGE,"E25.0"),sQuery(id+"F0.wireOp",EDGE,"E25.1"),sQuery(id+"F0.wireOp",EDGE,"E25.2"),sQuery(id+"F0.wireOp",EDGE,"E25.3"),sQuery(id+"F0.wireOp",EDGE,"E25.4"),sQuery(id+"F0.wireOp",EDGE,"E25.5"),sQuery(id+"F0.wireOp",EDGE,"E25.6"),sQuery(id+"F0.wireOp",EDGE,"E25.7")])],"isStart":false});
            var sketch = newSketch(context, id + "F16", { "sketchPlane" : qUnion([Q0])});
            skLineSegment(sketch, "E79.0", {"start": v(-70, 90) * mm, "end": v(70, 90) * mm});
            skArc(sketch, "E79.1", {"start": v(80, 80) * mm, "mid": v(77.07, 87.07) * mm, "end": v(70, 90) * mm});
            skLineSegment(sketch, "E79.2", {"start": v(80, -80) * mm, "end": v(80, 80) * mm});
            skArc(sketch, "E79.3", {"start": v(60, 40.3) * mm, "mid": v(58.99, 44.68) * mm, "end": v(56.15, 48.18) * mm});
            skArc(sketch, "E79.4", {"start": v(56.15, 48.18) * mm, "mid": v(0, 67.5) * mm, "end": v(-56.15, 48.18) * mm});
            skCircle(sketch, "E79.5", {"center": v(60, 67.5) * mm, "radius": 4 * mm});
            skCircle(sketch, "E79.6", {"center": v(-60, 67.5) * mm, "radius": 4 * mm});
            skArc(sketch, "E79.7", {"start": v(-56.15, 48.18) * mm, "mid": v(-58.99, 44.68) * mm, "end": v(-60, 40.3) * mm});
            skLineSegment(sketch, "E79.8", {"start": v(-60, 40.3) * mm, "end": v(-60, -40.3) * mm});
            skArc(sketch, "E79.9", {"start": v(-56.15, -48.18) * mm, "mid": v(0, -67.5) * mm, "end": v(56.15, -48.18) * mm});
            skLineSegment(sketch, "E79.10", {"start": v(60, 40.3) * mm, "end": v(60, -40.3) * mm});
            skArc(sketch, "E79.11", {"start": v(-60, -40.3) * mm, "mid": v(-58.99, -44.68) * mm, "end": v(-56.15, -48.18) * mm});
            skArc(sketch, "E79.12", {"start": v(56.15, -48.18) * mm, "mid": v(58.99, -44.68) * mm, "end": v(60, -40.3) * mm});
            skArc(sketch, "E79.13", {"start": v(-70, 90) * mm, "mid": v(-77.07, 87.07) * mm, "end": v(-80, 80) * mm});
            skLineSegment(sketch, "E79.14", {"start": v(-80, -80) * mm, "end": v(-80, 80) * mm});
            skArc(sketch, "E79.15", {"start": v(-80, -80) * mm, "mid": v(-77.07, -87.07) * mm, "end": v(-70, -90) * mm});
            skLineSegment(sketch, "E79.16", {"start": v(-70, -90) * mm, "end": v(70, -90) * mm});
            skArc(sketch, "E79.17", {"start": v(70, -90) * mm, "mid": v(77.07, -87.07) * mm, "end": v(80, -80) * mm});
            skPoint(sketch, "E80.endSnap0", {"position": v(0, 90) * mm});
            skLineSegment(sketch, "E81", {"start": v(0, 90) * mm, "end": v(0, 120) * mm});
            skCircle(sketch, "E82", {"center": v(0, 120) * mm, "radius": 6 * mm});
            skLineSegment(sketch, "E83", {"start": v(14.56, 108) * mm, "end": v(32.56, 90) * mm});
            skLineSegment(sketch, "E84", {"start": v(14.56, 108) * mm, "end": v(14.56, 120) * mm});
            skArc(sketch, "E85", {"start": v(14.56, 120) * mm, "mid": v(-0.44, 135) * mm, "end": v(-15.44, 120) * mm});
            skLineSegment(sketch, "E86", {"start": v(-15.44, 108) * mm, "end": v(-15.44, 120) * mm});
            skLineSegment(sketch, "E87", {"start": v(-15.44, 108) * mm, "end": v(-33.44, 90) * mm});
            skLineSegment(sketch, "E88", {"start": v(-80, 0) * mm, "end": v(80, 0) * mm, "construction": true});
            skLineSegment(sketch, "E89.MirrorCS", {"start": v(14.56, -108) * mm, "end": v(32.56, -90) * mm});
            skLineSegment(sketch, "E90.MirrorCS", {"start": v(-15.44, -108) * mm, "end": v(-33.44, -90) * mm});
            skLineSegment(sketch, "E91.MirrorCS", {"start": v(-15.44, -108) * mm, "end": v(-15.44, -120) * mm});
            skPoint(sketch, "E92.MirrorP", {"position": v(0, -90) * mm});
            skLineSegment(sketch, "E93.MirrorCS", {"start": v(14.56, -108) * mm, "end": v(14.56, -120) * mm});
            skArc(sketch, "E94.MirrorCS", {"start": v(14.56, -120) * mm, "mid": v(-0.44, -135) * mm, "end": v(-15.44, -120) * mm});
            skCircle(sketch, "E95.MirrorC", {"center": v(0, -120) * mm, "radius": 6 * mm});
            skLineSegment(sketch, "E96.MirrorCS", {"start": v(0, -90) * mm, "end": v(0, -120) * mm});
            skSolve(sketch);
        }
        {
            var Q0;
            {var subQ7=sQuery(id+"F16.wireOp",EDGE,"E79.1");Q0=makeQuery(id+"F16.imprint","IMPRINT",FACE,{"disambiguationData":[TD([[makeQuery(id+"F16.imprint","IMPRINT",EDGE,{"derivedFrom":subQ7}),1.0]])]});}
            var Q1;
            Q1=makeQuery(id+"F16.imprint","IMPRINT",FACE,{"disambiguationData":[TD([[makeQuery(id+"F16.imprint","IMPRINT",EDGE,{"derivedFrom":sQuery(id+"F16.wireOp",EDGE,"E82")}),-1.0]])]});
            var Q2;
            Q2=makeQuery(id+"F16.imprint","IMPRINT",FACE,{"disambiguationData":[TD([[makeQuery(id+"F16.imprint","IMPRINT",EDGE,{"derivedFrom":sQuery(id+"F16.wireOp",EDGE,"E91.MirrorCS")}),1.0]])]});
            extrude(context, id + "F17", {"entities" : qUnion([Q0, Q1, Q2]), "depth" : 3 * mm});
        }
    });
